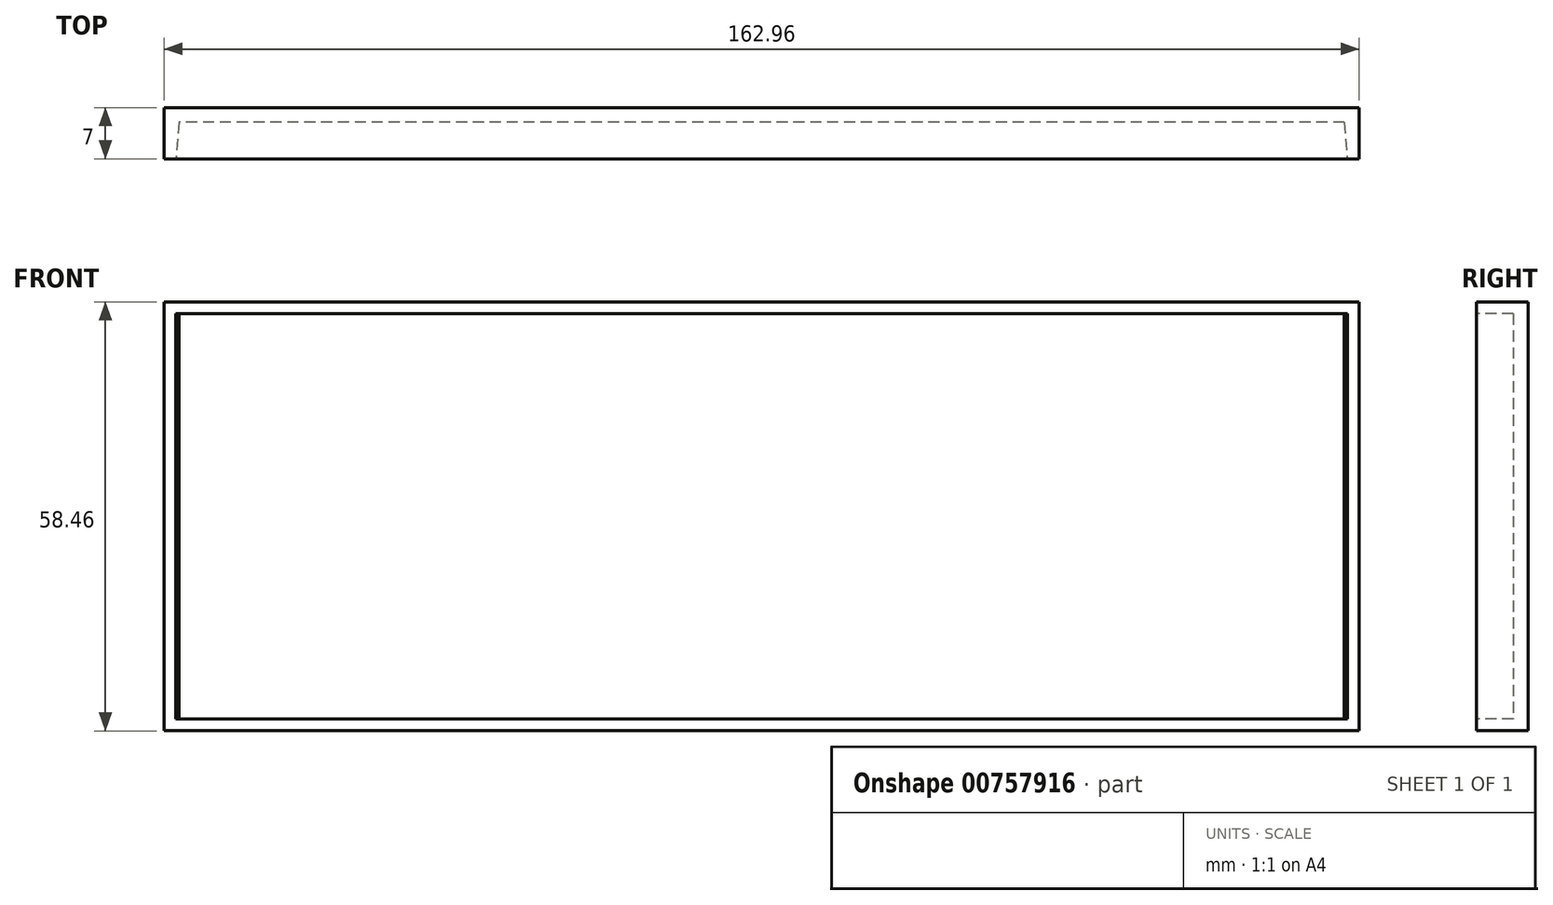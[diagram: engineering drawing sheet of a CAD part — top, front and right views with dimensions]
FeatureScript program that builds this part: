
annotation { "Feature Type Name" : "Feature", "Feature Type Description" : "" }
export const myFeature = defineFeature(function(context is Context, id is Id, definition is map)
    precondition{}
    {
        {
            var Q0;
            Q0=qCreatedBy(makeId("Front.planeOp"),FACE);
            var sketch = newSketch(context, id + "F0", { "sketchPlane" : qUnion([Q0])});
            skLineSegment(sketch, "E0.bottom", {"start": v(-81.47, 29.23) * mm, "end": v(81.47, 29.23) * mm});
            skLineSegment(sketch, "E0.top", {"start": v(-81.47, -29.23) * mm, "end": v(81.47, -29.23) * mm});
            skLineSegment(sketch, "E0.left", {"start": v(-81.47, 29.23) * mm, "end": v(-81.47, -29.23) * mm});
            skLineSegment(sketch, "E0.right", {"start": v(81.47, 29.23) * mm, "end": v(81.47, -29.23) * mm});
            skSolve(sketch);
        }
        {
            var Q0;
            Q0 = qSketchRegion(id + "F0", true);
            extrude(context, id + "F1", {"entities" : qUnion([Q0]), "depth" : 7 * mm, "offsetDistance" : 25 * mm});
        }
        {
            var Q0;
            Q0=makeQuery(id+"F1.opExtrude","CAP_FACE",FACE,{"disambiguationData":[OSD([sQuery(id+"F0.wireOp",EDGE,"E0.bottom"),sQuery(id+"F0.wireOp",EDGE,"E0.top"),sQuery(id+"F0.wireOp",EDGE,"E0.left"),sQuery(id+"F0.wireOp",EDGE,"E0.right")])],"isStart":false});
            var sketch = newSketch(context, id + "F2", { "sketchPlane" : qUnion([Q0])});
            skLineSegment(sketch, "E1.bottom", {"start": v(-79.88, 27.62) * mm, "end": v(79.87, 27.62) * mm});
            skLineSegment(sketch, "E1.top", {"start": v(-79.88, -27.62) * mm, "end": v(79.87, -27.62) * mm});
            skLineSegment(sketch, "E1.left", {"start": v(-79.88, 27.62) * mm, "end": v(-79.88, -27.62) * mm});
            skLineSegment(sketch, "E1.right", {"start": v(79.87, 27.62) * mm, "end": v(79.87, -27.62) * mm});
            skSolve(sketch);
        }
        {
            var Q0;
            Q0 = qSketchRegion(id + "F2", true);
            extrude(context, id + "F3", {"entities" : qUnion([Q0]), "operationType" : NewBodyOperationType.REMOVE, "oppositeDirection" : true, "depth" : 5 * mm, "offsetDistance" : 25 * mm, "hasDraft" : true, "draftAngle" : 5 * degree, "draftPullDirection" : true});
        }
        {
            var Q0;
            Q0=makeQuery(id+"F1.opExtrude","CAP_FACE",FACE,{"disambiguationData":[OSD([sQuery(id+"F0.wireOp",EDGE,"E0.bottom"),sQuery(id+"F0.wireOp",EDGE,"E0.top"),sQuery(id+"F0.wireOp",EDGE,"E0.left"),sQuery(id+"F0.wireOp",EDGE,"E0.right")])],"isStart":false});
            var sketch = newSketch(context, id + "F4", { "sketchPlane" : qUnion([Q0])});
            skLineSegment(sketch, "E2.bottom", {"start": v(-79.44, 27.62) * mm, "end": v(79.44, 27.62) * mm});
            skLineSegment(sketch, "E2.top", {"start": v(-79.44, -27.62) * mm, "end": v(79.44, -27.62) * mm});
            skLineSegment(sketch, "E2.left", {"start": v(-79.44, 27.62) * mm, "end": v(-79.44, -27.62) * mm});
            skLineSegment(sketch, "E2.right", {"start": v(79.44, 27.62) * mm, "end": v(79.44, -27.62) * mm});
            skSolve(sketch);
        }
        {
            var Q0;
            Q0 = qSketchRegion(id + "F4", true);
            var Q1;
            Q1=makeQuery(id+"F3.boolean.opBoolean","COPY",FACE,{"derivedFrom":makeQuery(id+"F3.opExtrude","CAP_FACE",FACE,{"disambiguationData":[OSD([sQuery(id+"F2.wireOp",EDGE,"E1.bottom"),sQuery(id+"F2.wireOp",EDGE,"E1.top"),sQuery(id+"F2.wireOp",EDGE,"E1.left"),sQuery(id+"F2.wireOp",EDGE,"E1.right")])],"isStart":false})});
            extrude(context, id + "F5", {"entities" : qUnion([Q0]), "operationType" : NewBodyOperationType.REMOVE, "endBound" : BoundingType.UP_TO_SURFACE, "oppositeDirection" : true, "depth" : 25 * mm, "endBoundEntityFace" : qUnion([Q1]), "offsetDistance" : 25 * mm});
        }
        {
            var Q0;
            {var subQ1=sQuery(id+"F2.wireOp",EDGE,"E1.top");Q0=makeQuery(id+"F5.boolean.opBoolean","COPY",FACE,{"disambiguationData":[TD([makeQuery(id+"F3.boolean.opBoolean","COPY",FACE,{"derivedFrom":makeQuery(id+"F3.opExtrude","SWEPT_FACE",FACE,{"disambiguationData":[OSD([subQ1])]})})])],"derivedFrom":makeQuery(id+"F5.opExtrude","SWEPT_FACE",FACE,{"disambiguationData":[OSD([sQuery(id+"F4.wireOp",EDGE,"E2.left")])]})});}
            var Q1;
            {var subQ1=sQuery(id+"F2.wireOp",EDGE,"E1.bottom");Q1=makeQuery(id+"F5.boolean.opBoolean","COPY",FACE,{"disambiguationData":[TD([makeQuery(id+"F3.boolean.opBoolean","COPY",FACE,{"derivedFrom":makeQuery(id+"F3.opExtrude","SWEPT_FACE",FACE,{"disambiguationData":[OSD([subQ1])]})})])],"derivedFrom":makeQuery(id+"F5.opExtrude","SWEPT_FACE",FACE,{"disambiguationData":[OSD([sQuery(id+"F4.wireOp",EDGE,"E2.left")])]})});}
            var Q2;
            Q2=makeQuery(id+"F3.boolean.opBoolean","COPY",FACE,{"derivedFrom":makeQuery(id+"F3.opExtrude","SWEPT_FACE",FACE,{"disambiguationData":[OSD([sQuery(id+"F2.wireOp",EDGE,"E1.left")])]})});
            extrude(context, id + "F6", {"entities" : qUnion([Q0, Q1]), "operationType" : NewBodyOperationType.REMOVE, "endBound" : BoundingType.UP_TO_SURFACE, "oppositeDirection" : true, "depth" : 25 * mm, "endBoundEntityFace" : qUnion([Q2]), "offsetDistance" : 25 * mm});
        }
        {
            var Q0;
            {var subQ1=sQuery(id+"F2.wireOp",EDGE,"E1.bottom");Q0=makeQuery(id+"F5.boolean.opBoolean","COPY",FACE,{"disambiguationData":[TD([makeQuery(id+"F3.boolean.opBoolean","COPY",FACE,{"derivedFrom":makeQuery(id+"F3.opExtrude","SWEPT_FACE",FACE,{"disambiguationData":[OSD([subQ1])]})})])],"derivedFrom":makeQuery(id+"F5.opExtrude","SWEPT_FACE",FACE,{"disambiguationData":[OSD([sQuery(id+"F4.wireOp",EDGE,"E2.right")])]})});}
            var Q1;
            {var subQ1=sQuery(id+"F2.wireOp",EDGE,"E1.top");Q1=makeQuery(id+"F5.boolean.opBoolean","COPY",FACE,{"disambiguationData":[TD([makeQuery(id+"F3.boolean.opBoolean","COPY",FACE,{"derivedFrom":makeQuery(id+"F3.opExtrude","SWEPT_FACE",FACE,{"disambiguationData":[OSD([subQ1])]})})])],"derivedFrom":makeQuery(id+"F5.opExtrude","SWEPT_FACE",FACE,{"disambiguationData":[OSD([sQuery(id+"F4.wireOp",EDGE,"E2.right")])]})});}
            var Q2;
            Q2=makeQuery(id+"F3.boolean.opBoolean","COPY",FACE,{"derivedFrom":makeQuery(id+"F3.opExtrude","SWEPT_FACE",FACE,{"disambiguationData":[OSD([sQuery(id+"F2.wireOp",EDGE,"E1.right")])]})});
            extrude(context, id + "F7", {"entities" : qUnion([Q0, Q1]), "operationType" : NewBodyOperationType.REMOVE, "endBound" : BoundingType.UP_TO_SURFACE, "oppositeDirection" : true, "depth" : 25 * mm, "endBoundEntityFace" : qUnion([Q2]), "offsetDistance" : 25 * mm});
        }
    });
